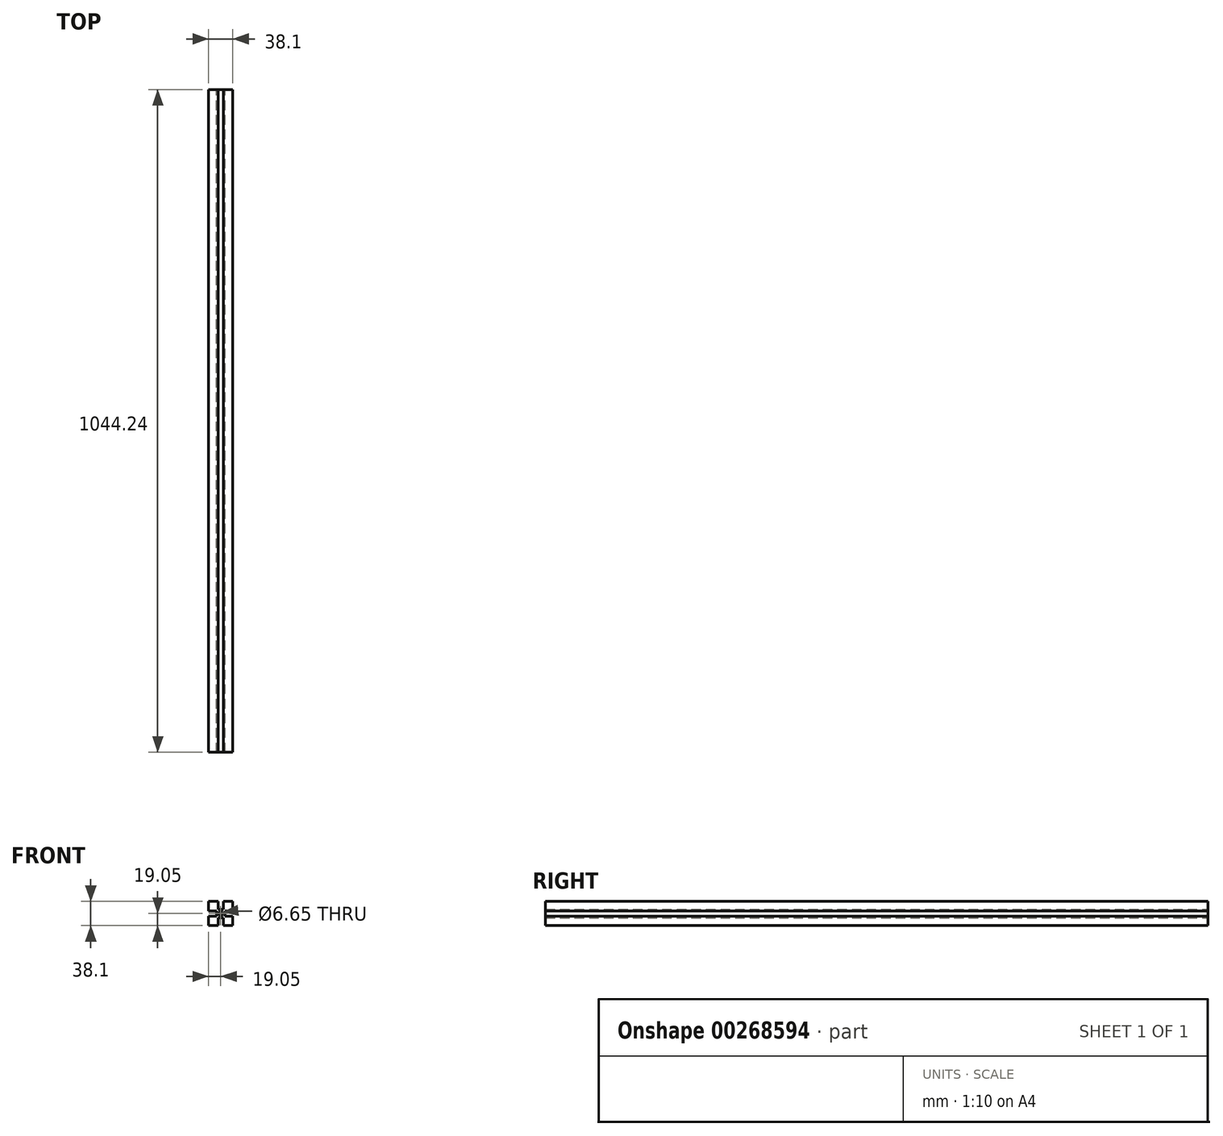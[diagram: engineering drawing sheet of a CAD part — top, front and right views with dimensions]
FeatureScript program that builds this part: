
annotation { "Feature Type Name" : "Feature", "Feature Type Description" : "" }
export const myFeature = defineFeature(function(context is Context, id is Id, definition is map)
    precondition{}
    {
        {
            var Q0;
            Q0=qCreatedBy(makeId("Front.planeOp"),FACE);
            var sketch = newSketch(context, id + "F0", { "sketchPlane" : qUnion([Q0])});
            skPoint(sketch, "E0.middle", {"position": v(0, 0) * mm});
            skCircle(sketch, "E1", {"center": v(0, 0) * mm, "radius": 3.33 * mm});
            skLineSegment(sketch, "E2.top", {"start": v(4.06, 6.76) * mm, "end": v(-4.06, 6.76) * mm});
            skLineSegment(sketch, "E3", {"start": v(-4.06, 19.05) * mm, "end": v(-4.06, 6.76) * mm});
            skLineSegment(sketch, "E4", {"start": v(4.06, 19.05) * mm, "end": v(4.06, 6.76) * mm});
            skLineSegment(sketch, "E5", {"start": v(-19.05, 4.06) * mm, "end": v(-19.05, 19.05) * mm});
            skLineSegment(sketch, "E6", {"start": v(-19.05, 19.05) * mm, "end": v(-4.06, 19.05) * mm});
            skLineSegment(sketch, "E7", {"start": v(4.06, 19.05) * mm, "end": v(19.05, 19.05) * mm});
            skLineSegment(sketch, "E8", {"start": v(19.05, 19.05) * mm, "end": v(19.05, 4.06) * mm});
            skLineSegment(sketch, "E9", {"start": v(-19.05, -4.06) * mm, "end": v(-19.05, -19.05) * mm});
            skLineSegment(sketch, "E10", {"start": v(-19.05, -19.05) * mm, "end": v(-4.06, -19.05) * mm});
            skLineSegment(sketch, "E11", {"start": v(4.06, -19.05) * mm, "end": v(19.05, -19.05) * mm});
            skLineSegment(sketch, "E12", {"start": v(19.05, -19.05) * mm, "end": v(19.05, -4.06) * mm});
            skLineSegment(sketch, "E13.trimOffspring", {"start": v(6.76, 4.06) * mm, "end": v(19.05, 4.06) * mm});
            skLineSegment(sketch, "E14", {"start": v(19.05, -4.06) * mm, "end": v(6.76, -4.06) * mm});
            skLineSegment(sketch, "E15", {"start": v(6.76, 4.06) * mm, "end": v(6.76, -4.06) * mm});
            skLineSegment(sketch, "E16", {"start": v(-19.05, -4.06) * mm, "end": v(-6.76, -4.06) * mm});
            skLineSegment(sketch, "E17", {"start": v(-4.06, -19.05) * mm, "end": v(-4.06, -6.76) * mm});
            skLineSegment(sketch, "E18", {"start": v(-19.05, 4.06) * mm, "end": v(-6.76, 4.06) * mm});
            skLineSegment(sketch, "E19", {"start": v(-6.76, 4.06) * mm, "end": v(-6.76, -4.06) * mm});
            skLineSegment(sketch, "E20", {"start": v(4.06, -19.05) * mm, "end": v(4.06, -6.76) * mm});
            skLineSegment(sketch, "E21", {"start": v(4.06, -6.76) * mm, "end": v(-4.06, -6.76) * mm});
            skSolve(sketch);
        }
        {
            var Q0;
            Q0=makeQuery(id+"F0.imprint","IMPRINT",FACE,{"disambiguationData":[TD([[makeQuery(id+"F0.imprint","IMPRINT",EDGE,{"derivedFrom":sQuery(id+"F0.wireOp",EDGE,"E1")}),-1.0]])]});
            extrude(context, id + "F1", {"entities" : qUnion([Q0]), "depth" : 1044.24 * mm});
        }
    });
